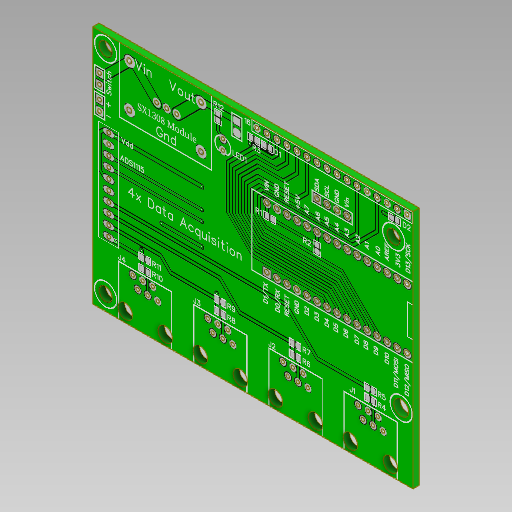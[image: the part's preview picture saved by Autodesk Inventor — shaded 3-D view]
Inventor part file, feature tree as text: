
AUTODESK INVENTOR PART (.ipt)
format: ipt  version: 2020 (Build 240168000, 168)  size: 644,096 bytes
history: native  units: in
note: dims shown in document units (in); Inventor stores cm internally (conversion verified against a paired STEP export)
features: other x4, sketch x4, extrude x2
ambient origin geometry x8: Origin, YZ Plane, XZ Plane, XY Plane, X Axis, Y Axis, Z Axis, Center Point
bodies: Solid1 (feature_tree)
feature tree (10):
  extrude  "Extrusion1"  Depth=2.4in
  other  "Decal1"
  other  "Decal2"
  extrude  "Extrusion2"  Depth=0.0625in
  sketch  "Sketch1"  dims[d0=3.2in d1=2.4in]
  sketch  "Sketch2"  dims[d2=0.0625in d3=0.0in d10=0.04in]
  other  "Image1"
  sketch  "Sketch3"  dims[d11=0.05in]
  other  "Image2"
  sketch  "Sketch4"  dims[d12=0.04in d13=0.04in d14=0.655in d15=1.74in d16=5.9055in d18=0.1in d19=0.7874in d21=0.6in d24=0.055in d25=1.64in d26=6.2992in d28=0.1in d29=0.3937in d31=1.0in d33=0.1125in d34=0.365in d35=0.7874in d37=0.7175in d38=0.7874in d40=0.4275in d43=0.0675in d44=0.3675in d45=0.23in d46=0.7874in d48=0.1in d49=0.3937in d51=1.0in d53=0.16in d54=0.8375in d55=3.937in d57=0.1in d58=0.3937in d60=1.0in d62=0.3987in d63=0.035in d64=1.95in d65=0.05in d66=0.1in d67=1.1811in d69=0.1in d70=0.3937in d72=1.0in d74=1.5748in d76=0.75in d77=0.3937in d79=1.0in d81=0.13in d82=0.1275in d83=0.1275in d84=0.3675in d85=2.242in d86=0.05in d87=1.5748in d89=0.1in d90=0.3937in d92=1.0in d94=0.13in d95=0.315in d96=3.005in d97=0.145in d98=0.1in d99=0.325in d100=0.7874in d102=0.4in d103=0.3937in d105=1.0in d107=1.5748in d109=0.75in d110=0.3937in d112=1.0in d114=0.13in d115=0.15in d116=0.15in d117=0.1175in d118=0.6425in d119=0.035in d120=0.32in d121=1.3in d122=0.7874in d124=0.1in d125=0.3937in d127=1.0in d129=0.0in d130=0.0in d131=0.04in d132=0.3375in d133=0.6385in d134=1.1811in d136=0.1in d137=0.3937in d139=1.0in]
